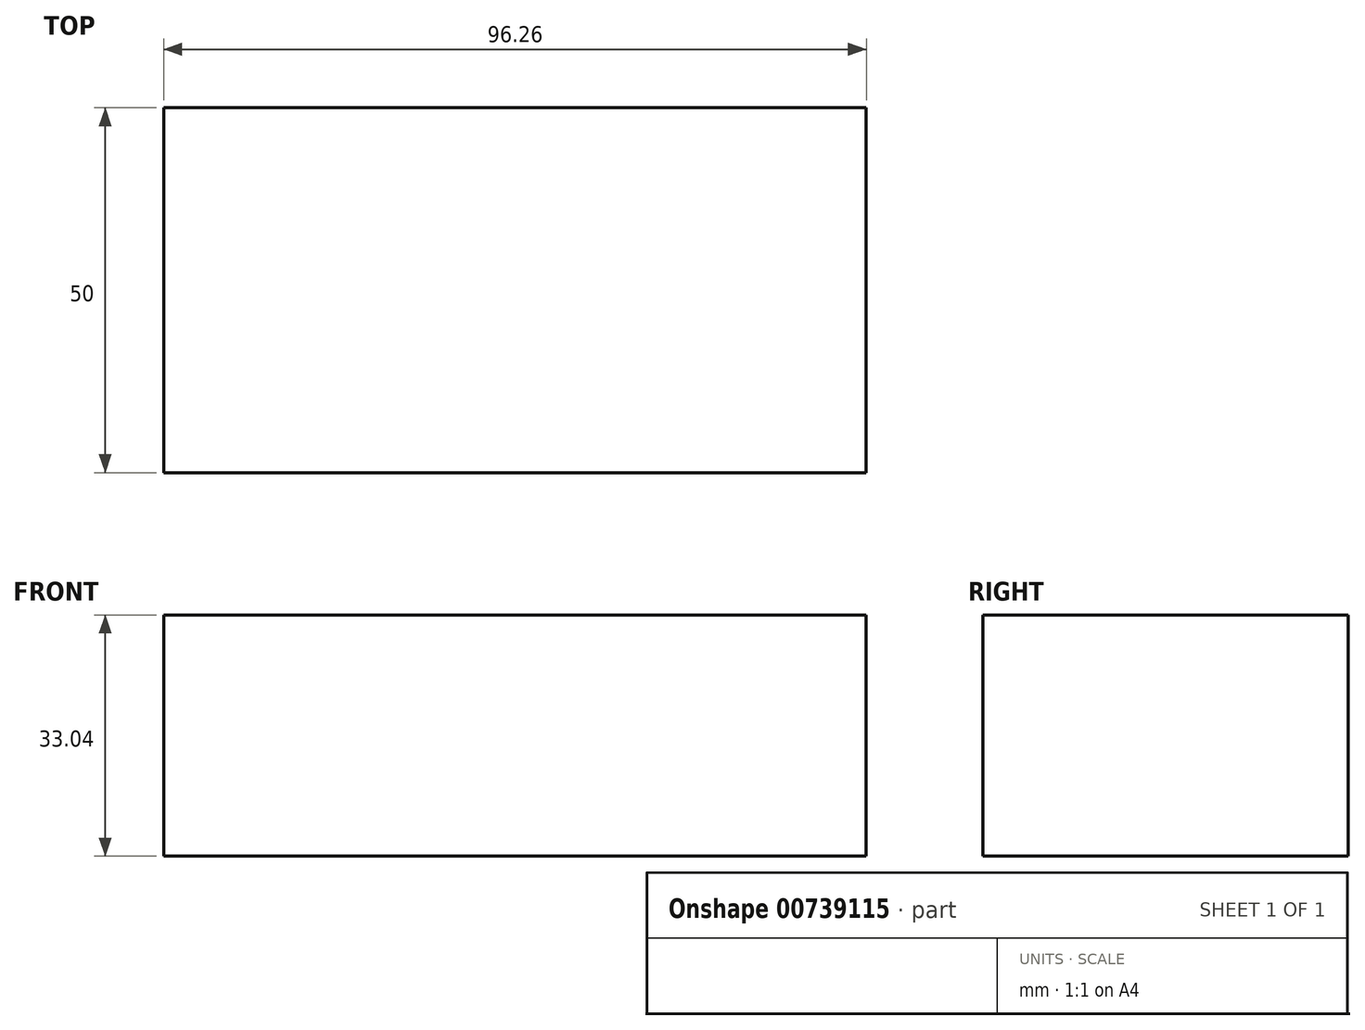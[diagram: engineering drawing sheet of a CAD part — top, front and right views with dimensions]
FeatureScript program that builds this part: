
annotation { "Feature Type Name" : "Feature", "Feature Type Description" : "" }
export const myFeature = defineFeature(function(context is Context, id is Id, definition is map)
    precondition{}
    {
        {
            var Q0;
            Q0=qCreatedBy(makeId("Front.planeOp"),FACE);
            var sketch = newSketch(context, id + "F0", { "sketchPlane" : qUnion([Q0])});
            skLineSegment(sketch, "E0.bottom", {"start": v(-48.13, 16.52) * mm, "end": v(48.13, 16.52) * mm});
            skLineSegment(sketch, "E0.top", {"start": v(-48.13, -16.52) * mm, "end": v(48.13, -16.52) * mm});
            skLineSegment(sketch, "E0.left", {"start": v(-48.13, 16.52) * mm, "end": v(-48.13, -16.52) * mm});
            skLineSegment(sketch, "E0.right", {"start": v(48.13, 16.52) * mm, "end": v(48.13, -16.52) * mm});
            skPoint(sketch, "E0.middle", {"position": v(0, 0) * mm});
            skSolve(sketch);
        }
        {
            var Q0;
            Q0=makeQuery(id+"F0.imprint","IMPRINT",FACE,{"disambiguationData":[TD([[makeQuery(id+"F0.imprint","IMPRINT",EDGE,{"derivedFrom":sQuery(id+"F0.wireOp",EDGE,"E0.bottom")}),-1.0]])]});
            extrude(context, id + "F1", {"entities" : qUnion([Q0]), "depth" : 50 * mm, "offsetDistance" : 25 * mm});
        }
    });
